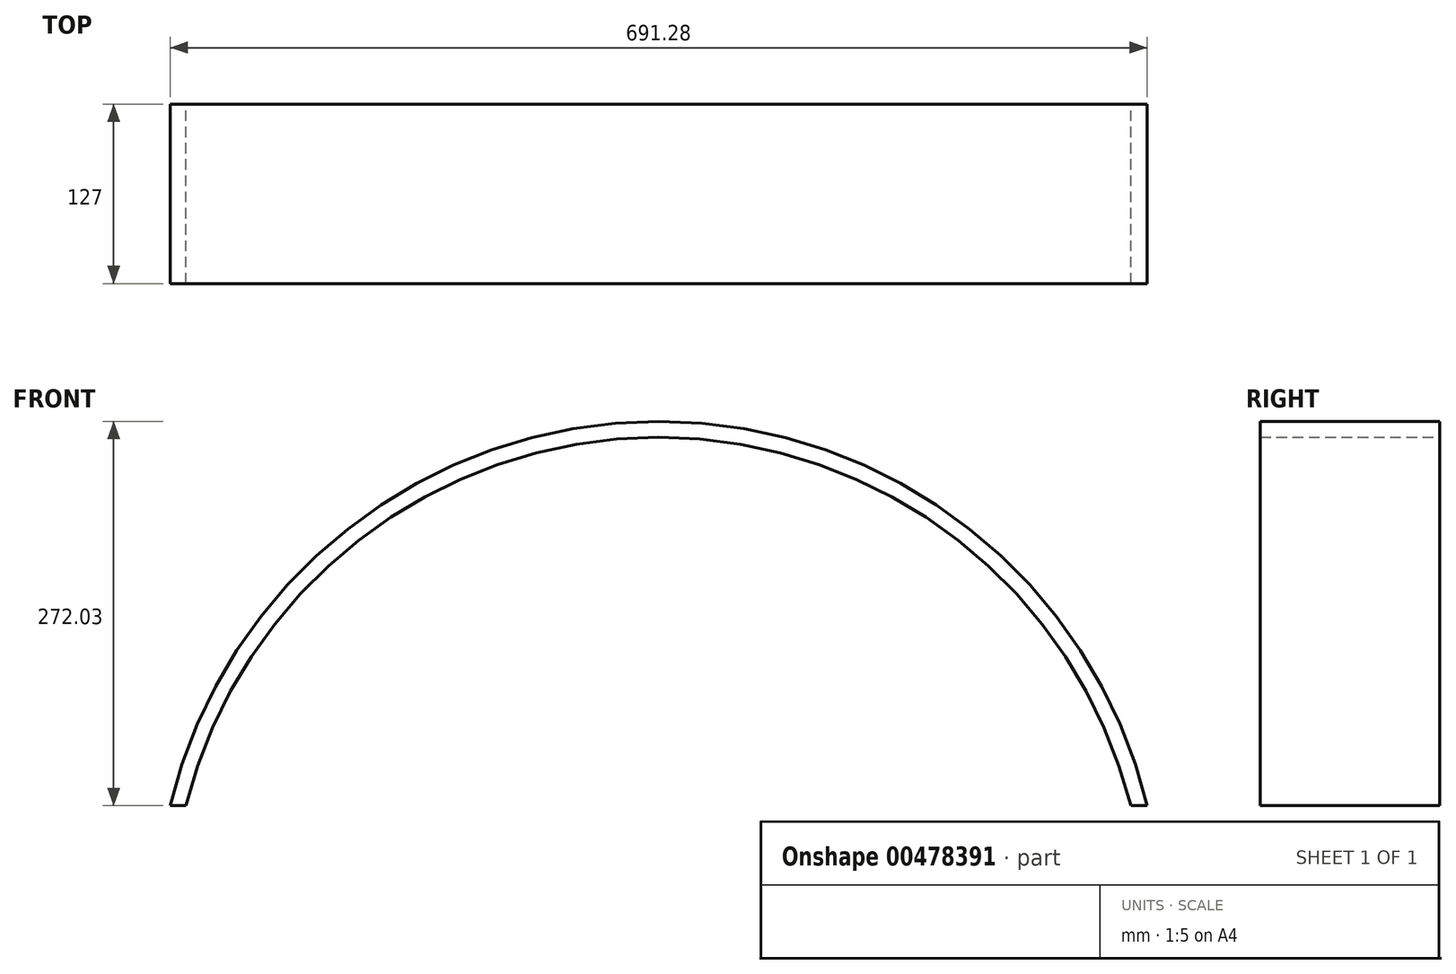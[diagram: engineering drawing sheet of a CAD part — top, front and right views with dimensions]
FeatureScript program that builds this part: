
annotation { "Feature Type Name" : "Feature", "Feature Type Description" : "" }
export const myFeature = defineFeature(function(context is Context, id is Id, definition is map)
    precondition{}
    {
        {
            var Q0;
            Q0=qCreatedBy(makeId("Front.planeOp"),FACE);
            var sketch = newSketch(context, id + "F0", { "sketchPlane" : qUnion([Q0])});
            skArc(sketch, "E0", {"start": v(691.28, 0) * mm, "mid": v(345.64, 272.03) * mm, "end": v(0, 0) * mm});
            skArc(sketch, "E1", {"start": v(679.77, 0) * mm, "mid": v(345.44, 260.73) * mm, "end": v(11.1, 0) * mm});
            skLineSegment(sketch, "E2", {"start": v(0, 0) * mm, "end": v(11.1, 0) * mm});
            skLineSegment(sketch, "E3", {"start": v(679.77, 0) * mm, "end": v(691.28, 0) * mm});
            skSolve(sketch);
        }
        {
            var Q0;
            Q0=makeQuery(id+"F0.imprint","IMPRINT",FACE,{"disambiguationData":[TD([[makeQuery(id+"F0.imprint","IMPRINT",EDGE,{"derivedFrom":sQuery(id+"F0.wireOp",EDGE,"E0")}),1.0]])]});
            extrude(context, id + "F1", {"entities" : qUnion([Q0]), "depth" : 127 * mm});
        }
    });
